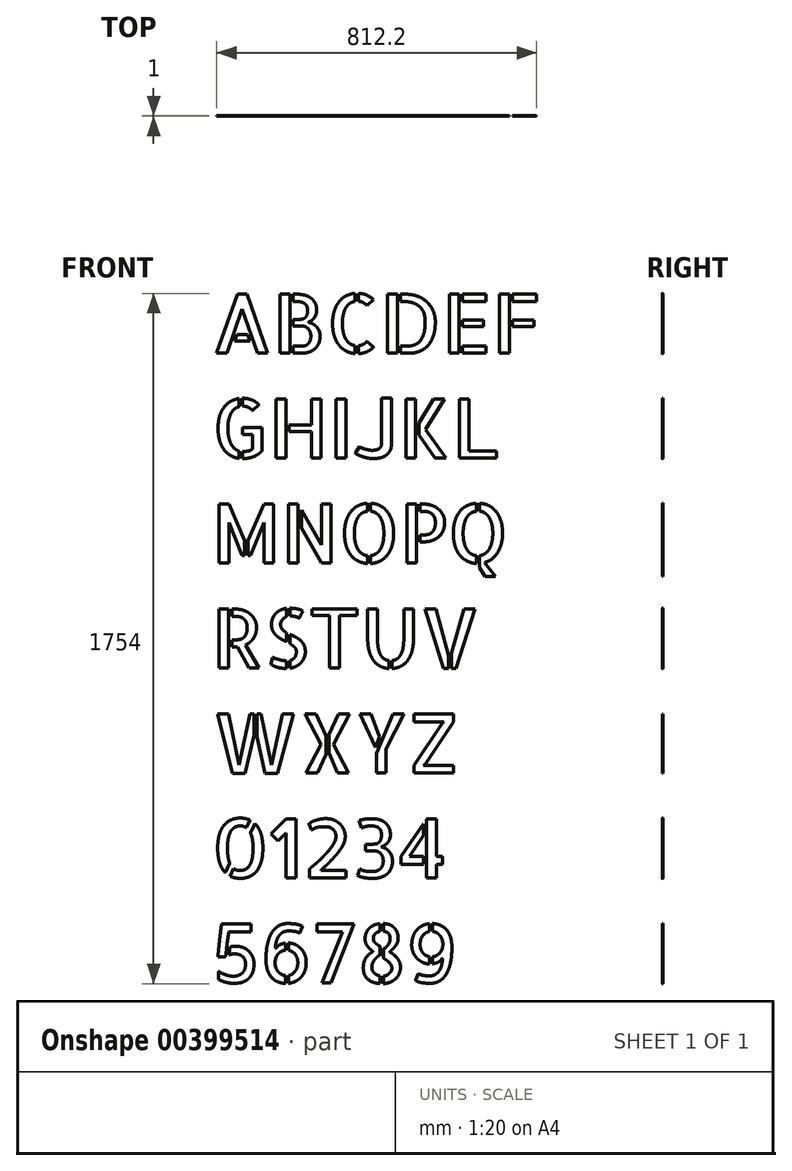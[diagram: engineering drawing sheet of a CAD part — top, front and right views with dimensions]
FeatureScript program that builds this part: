
annotation { "Feature Type Name" : "Feature", "Feature Type Description" : "" }
export const myFeature = defineFeature(function(context is Context, id is Id, definition is map)
    precondition{}
    {
        {
            var Q0;
            Q0=qCreatedBy(makeId("Front.planeOp"),FACE);
            var sketch = newSketch(context, id + "F0", { "sketchPlane" : qUnion([Q0])});
            skText(sketch, "E0", { "text": "ABCDEF\nGHIJKL\nMNOPQ\nRSTUV\nWXYZ\n01234\n56789", "fontName": "AllertaStencil-Regular.ttf"});
            const initialGuessF0  = {"E0": [-1.07812, 0.74531, 1, 0, 0.15]};
            skSetInitialGuess(sketch, initialGuessF0);
            skSolve(sketch);
        }
        {
            var Q0;
            Q0 = qSketchRegion(id + "F0", true);
            extrude(context, id + "F1", {"entities" : qUnion([Q0]), "depth" : 1 * mm});
        }
    });
